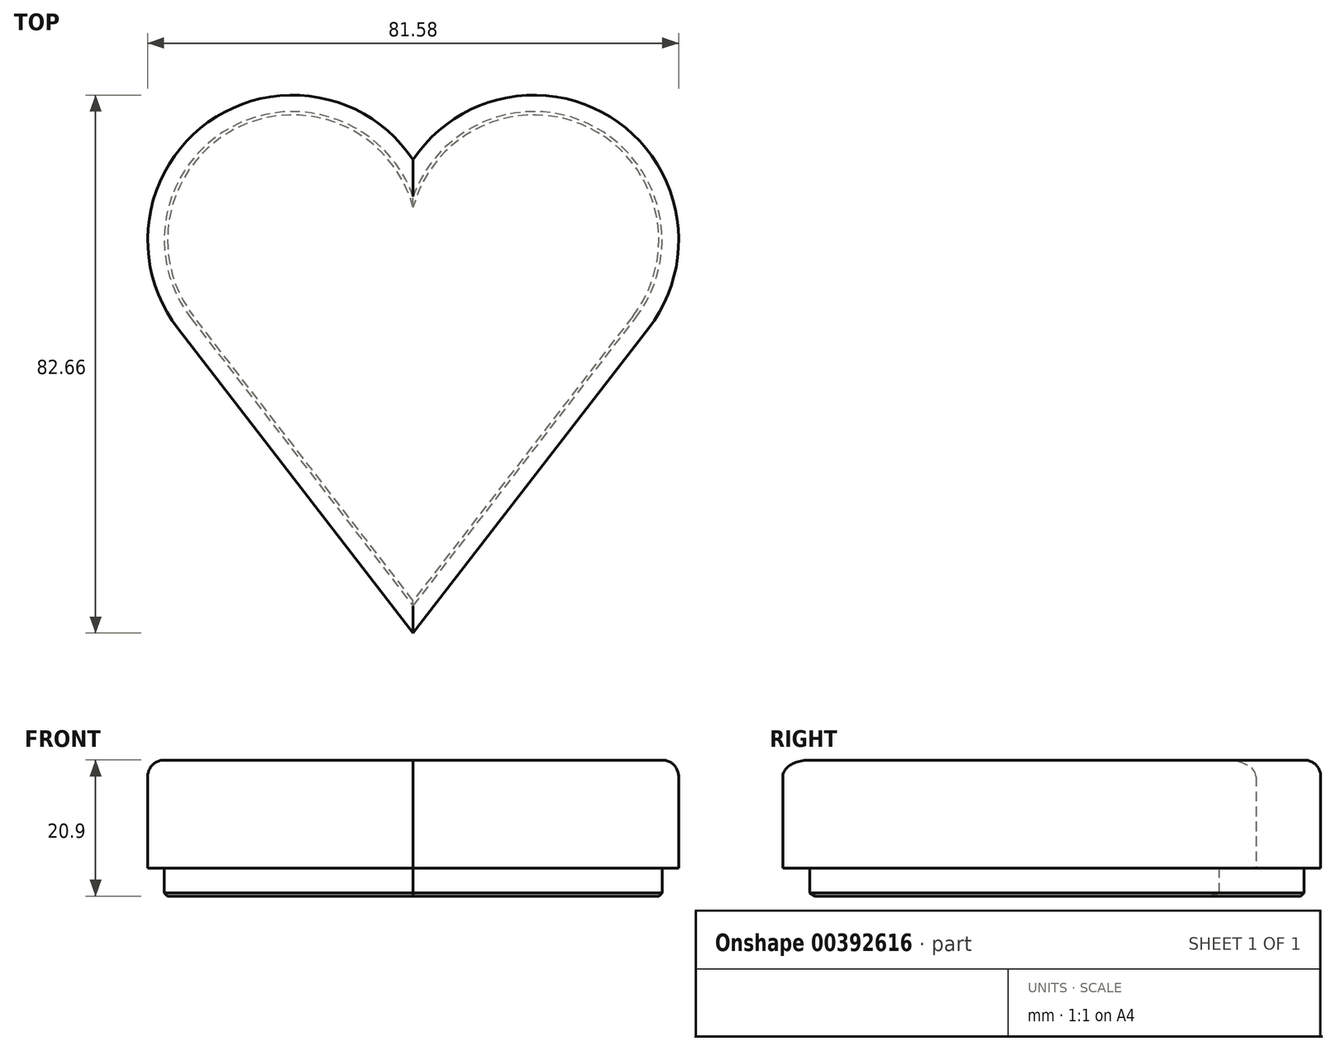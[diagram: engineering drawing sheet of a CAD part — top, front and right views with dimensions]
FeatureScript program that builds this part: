
annotation { "Feature Type Name" : "Feature", "Feature Type Description" : "" }
export const myFeature = defineFeature(function(context is Context, id is Id, definition is map)
    precondition{}
    {
        {
            var Q0;
            Q0=qCreatedBy(makeId("Top.planeOp"),FACE);
            var sketch = newSketch(context, id + "F0", { "sketchPlane" : qUnion([Q0])});
            skLineSegment(sketch, "E0", {"start": v(0, -46.8) * mm, "end": v(36.15, 0) * mm});
            skArc(sketch, "E1", {"start": v(36.15, 0) * mm, "mid": v(31.5, 31.69) * mm, "end": v(0, 25.9) * mm});
            skLineSegment(sketch, "E2", {"start": v(0, -46.8) * mm, "end": v(-36.15, 0) * mm});
            skArc(sketch, "E3", {"start": v(-36.15, 0) * mm, "mid": v(-31.5, 31.69) * mm, "end": v(0, 25.9) * mm});
            skSolve(sketch);
        }
        {
            var Q0;
            Q0=makeQuery(id+"F0.imprint","IMPRINT",FACE,{"disambiguationData":[TD([[makeQuery(id+"F0.imprint","IMPRINT",EDGE,{"derivedFrom":sQuery(id+"F0.wireOp",EDGE,"E0")}),1.0]])]});
            extrude(context, id + "F1", {"entities" : qUnion([Q0]), "depth" : 16.63 * mm});
        }
        {
            var Q0;
            Q0=makeQuery(id+"F1.opExtrude","CAP_FACE",FACE,{"disambiguationData":[OSD([sQuery(id+"F0.wireOp",EDGE,"E0"),sQuery(id+"F0.wireOp",EDGE,"E1"),sQuery(id+"F0.wireOp",EDGE,"E2"),sQuery(id+"F0.wireOp",EDGE,"E3")])],"isStart":false});
            fillet(context, id + "F2", {"entities" : qUnion([Q0]), "radius" : 2.54 * mm, "tangentPropagation" : true, "allowEdgeOverflow" : false});
        }
        {
            var Q0;
            Q0=makeQuery(id+"F1.opExtrude","CAP_FACE",FACE,{"disambiguationData":[OSD([sQuery(id+"F0.wireOp",EDGE,"E0"),sQuery(id+"F0.wireOp",EDGE,"E1"),sQuery(id+"F0.wireOp",EDGE,"E2"),sQuery(id+"F0.wireOp",EDGE,"E3")])],"isStart":false});
            extrude(context, id + "F3", {"entities" : qUnion([Q0]), "operationType" : NewBodyOperationType.ADD, "oppositeDirection" : true, "depth" : 20.9 * mm});
        }
        {
            var Q0;
            Q0=makeQuery(id+"F3.opExtrude","CAP_FACE",FACE,{"disambiguationData":[OSD([sQuery(id+"F0.wireOp",EDGE,"E0"),sQuery(id+"F0.wireOp",EDGE,"E1"),sQuery(id+"F0.wireOp",EDGE,"E2"),sQuery(id+"F0.wireOp",EDGE,"E3")])],"isStart":false});
            chamfer(context, id + "F4", {"entities" : qUnion([Q0]), "chamferType" : ChamferType.OFFSET_ANGLE, "width" : 0.5 * mm, "oppositeDirection" : false, "angle" : 45 * degree, "tangentPropagation" : true});
        }
    });
